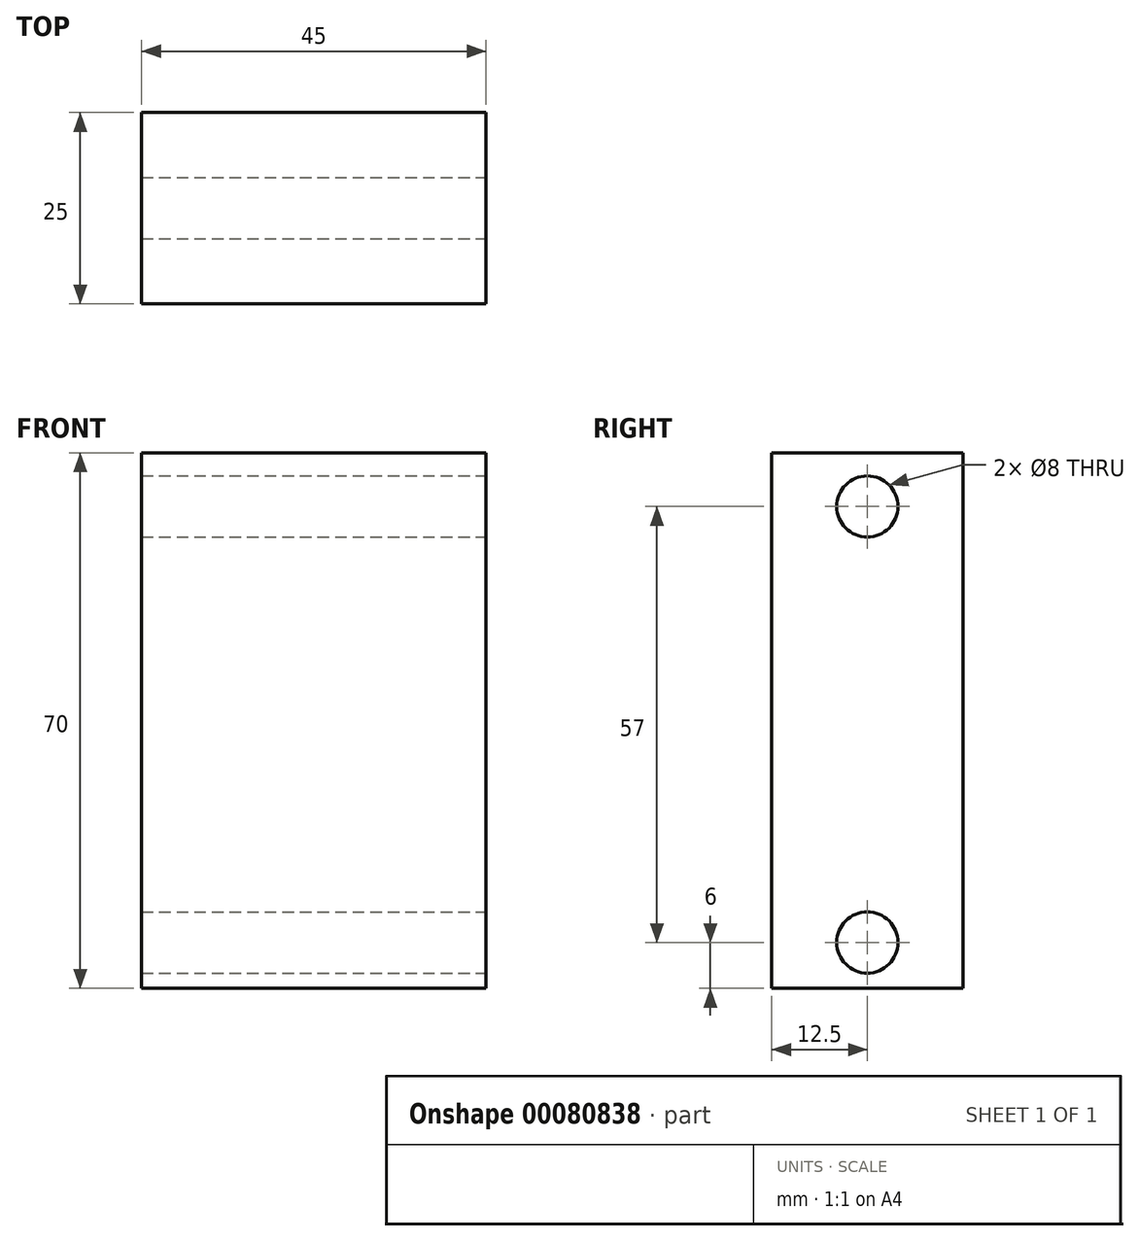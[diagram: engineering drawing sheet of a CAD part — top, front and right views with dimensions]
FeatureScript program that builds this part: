
annotation { "Feature Type Name" : "Feature", "Feature Type Description" : "" }
export const myFeature = defineFeature(function(context is Context, id is Id, definition is map)
    precondition{}
    {
        {
            var Q0;
            Q0=qCreatedBy(makeId("Front.planeOp"),FACE);
            var sketch = newSketch(context, id + "F0", { "sketchPlane" : qUnion([Q0])});
            skLineSegment(sketch, "E0.bottom", {"start": v(22.5, -35) * mm, "end": v(-22.5, -35) * mm});
            skLineSegment(sketch, "E0.top", {"start": v(22.5, 35) * mm, "end": v(-22.5, 35) * mm});
            skLineSegment(sketch, "E0.left", {"start": v(22.5, -35) * mm, "end": v(22.5, 35) * mm});
            skLineSegment(sketch, "E0.right", {"start": v(-22.5, -35) * mm, "end": v(-22.5, 35) * mm});
            skPoint(sketch, "E0.middle", {"position": v(0, 0) * mm});
            skSolve(sketch);
        }
        {
            var Q0;
            Q0=makeQuery(id+"F0.imprint","IMPRINT",FACE,{"disambiguationData":[TD([[makeQuery(id+"F0.imprint","IMPRINT",EDGE,{"derivedFrom":sQuery(id+"F0.wireOp",EDGE,"E0.bottom")}),-1.0]])]});
            extrude(context, id + "F1", {"entities" : qUnion([Q0]), "depth" : 25 * mm});
        }
        {
            var Q0;
            Q0=makeQuery(id+"F1.opExtrude","SWEPT_FACE",FACE,{"disambiguationData":[OSD([sQuery(id+"F0.wireOp",EDGE,"E0.left")])]});
            var sketch = newSketch(context, id + "F2", { "sketchPlane" : qUnion([Q0])});
            skLineSegment(sketch, "E1", {"start": v(-12.5, 35) * mm, "end": v(-12.5, 28) * mm, "construction": true});
            skLineSegment(sketch, "E2", {"start": v(-12.5, 28) * mm, "end": v(-12.5, -29) * mm, "construction": true});
            skCircle(sketch, "E3", {"center": v(-12.5, 28) * mm, "radius": 4 * mm});
            skCircle(sketch, "E4", {"center": v(-12.5, -29) * mm, "radius": 4 * mm});
            skSolve(sketch);
        }
        {
            var Q0;
            Q0=makeQuery(id+"F2.imprint","IMPRINT",FACE,{"disambiguationData":[TD([[makeQuery(id+"F2.imprint","IMPRINT",EDGE,{"derivedFrom":sQuery(id+"F2.wireOp",EDGE,"E3")}),1.0]])]});
            var Q1;
            Q1=makeQuery(id+"F2.imprint","IMPRINT",FACE,{"disambiguationData":[TD([[makeQuery(id+"F2.imprint","IMPRINT",EDGE,{"derivedFrom":sQuery(id+"F2.wireOp",EDGE,"E4")}),1.0]])]});
            extrude(context, id + "F3", {"entities" : qUnion([Q0, Q1]), "operationType" : NewBodyOperationType.REMOVE, "endBound" : BoundingType.THROUGH_ALL, "oppositeDirection" : true, "depth" : 25 * mm});
        }
    });
